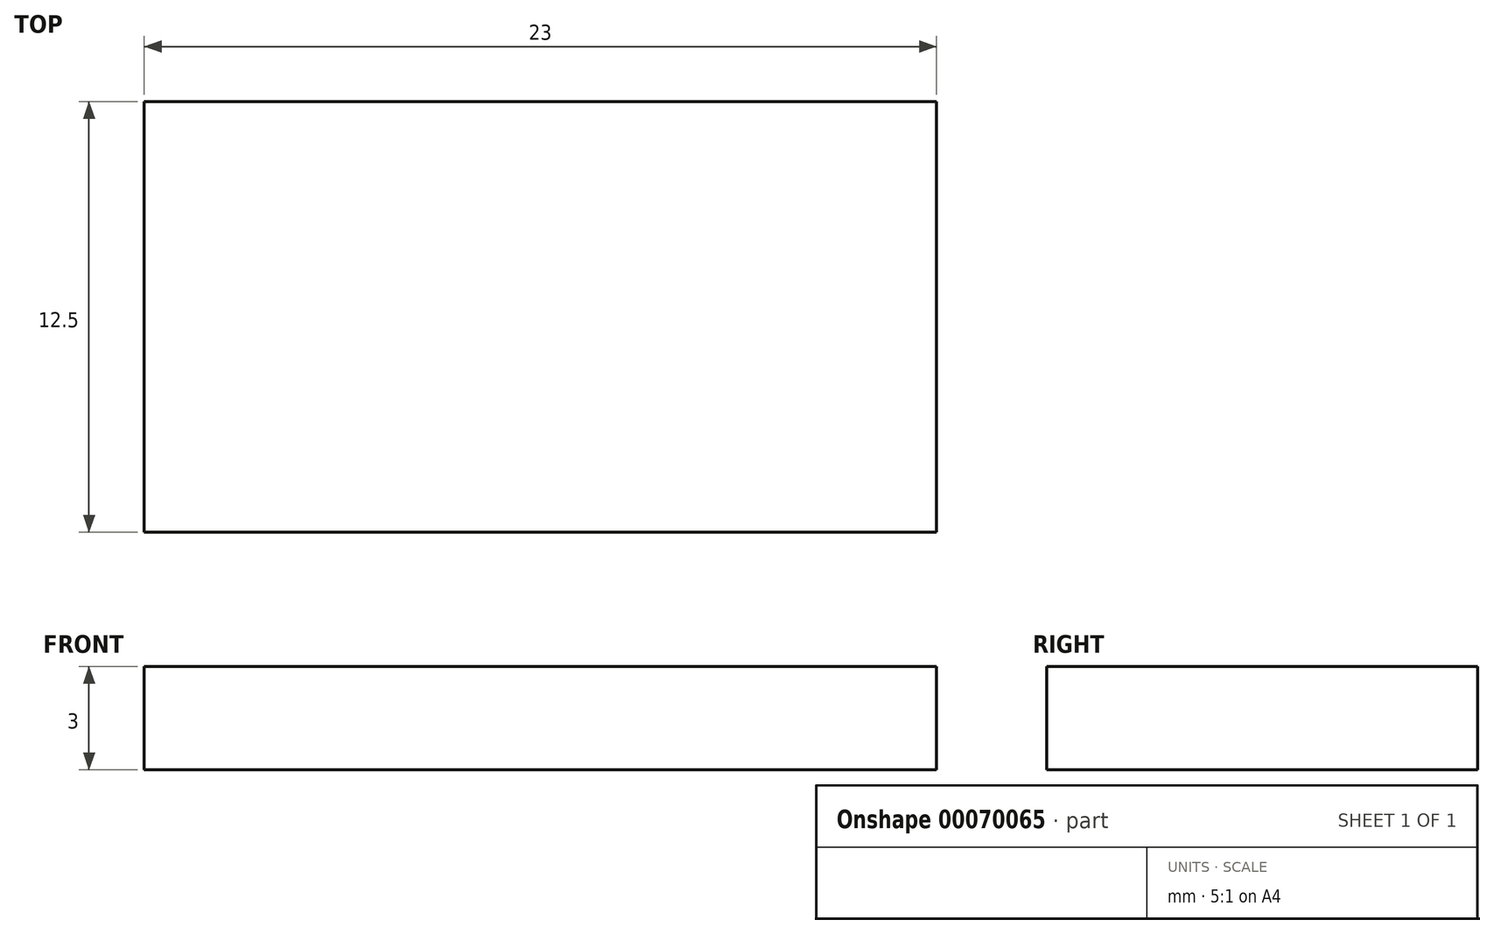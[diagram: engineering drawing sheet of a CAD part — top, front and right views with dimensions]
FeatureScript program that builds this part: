
annotation { "Feature Type Name" : "Feature", "Feature Type Description" : "" }
export const myFeature = defineFeature(function(context is Context, id is Id, definition is map)
    precondition{}
    {
        {
            var Q0;
            Q0=qCreatedBy(makeId("Top.planeOp"),FACE);
            var sketch = newSketch(context, id + "F0", { "sketchPlane" : qUnion([Q0])});
            skLineSegment(sketch, "E0.bottom", {"start": v(11.5, 6.25) * mm, "end": v(-11.5, 6.25) * mm});
            skLineSegment(sketch, "E0.top", {"start": v(11.5, -6.25) * mm, "end": v(-11.5, -6.25) * mm});
            skLineSegment(sketch, "E0.left", {"start": v(11.5, 6.25) * mm, "end": v(11.5, -6.25) * mm});
            skLineSegment(sketch, "E0.right", {"start": v(-11.5, 6.25) * mm, "end": v(-11.5, -6.25) * mm});
            skPoint(sketch, "E0.middle", {"position": v(0, 0) * mm});
            skSolve(sketch);
        }
        {
            var Q0;
            Q0 = qSketchRegion(id + "F0", true);
            extrude(context, id + "F1", {"entities" : qUnion([Q0]), "endBound" : BoundingType.SYMMETRIC, "depth" : 3 * mm});
        }
    });
